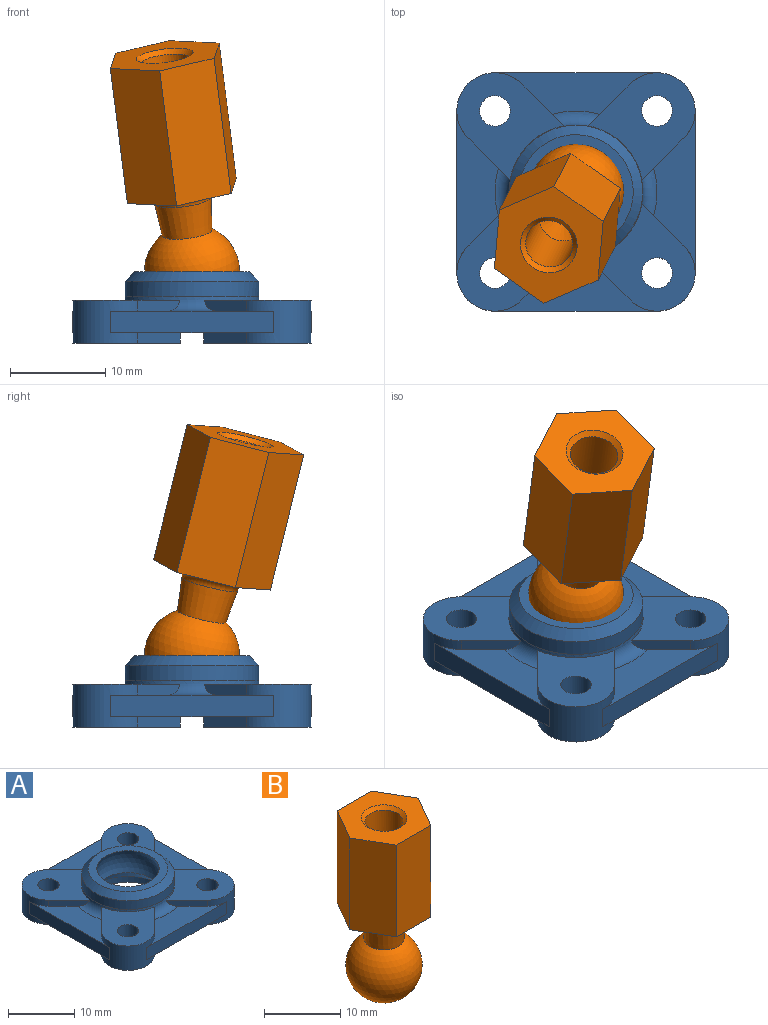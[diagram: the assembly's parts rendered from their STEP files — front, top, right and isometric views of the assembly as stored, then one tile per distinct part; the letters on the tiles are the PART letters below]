
ASSEMBLY  parts=2 mates=1
PART A: 54 faces, bbox 25.1x25.1x7.6 mm
  f0: cylinder r=4mm len=6.83mm, axis (0,0,-1), area 42.4mm2, adj f14,f15,f21,f28,f29,f30,f33,f34
  f1: cylinder r=4mm len=6.83mm, axis (0,0,-1), area 42.4mm2, adj f15,f19,f27,f32,f34,f35,f37,f46
  f2: cylinder r=4mm len=6.83mm, axis (0,0,-1), area 42.4mm2, adj f19,f20,f22,f31,f38,f39,f41,f42
  f3: cylinder r=4mm len=6.83mm, axis (0,0,-1), area 42.4mm2, adj f16,f17,f18,f21,f22,f29,f43,f44
  f4: cone r=5.81mm half-angle=45deg, axis (0,0,-1), area 120.4mm2, adj f12,f21,f22,f23,f24,f25,f26,f34
  f5: cylinder r=7mm len=14mm, axis (0,0,1), area 71.5mm2, adj f6,f7
  f6: cone r=6.5mm half-angle=45deg, axis (0,0,-1), area 57.8mm2, adj f5,f13
  f7: torus R=8.5mm, axis (0,0,-1), area 45.8mm2, adj f5,f14,f15,f16,f17,f18,f19,f20
  f8: cylinder r=1.6mm len=4.5mm, axis (0,0,-1), area 45.2mm2, adj f17,f48
  f9: cylinder r=1.6mm len=4.5mm, axis (0,0,-1), area 45.2mm2, adj f31,f38
  f10: cylinder r=1.6mm len=4.5mm, axis (0,0,-1), area 45.2mm2, adj f32,f37
  f11: cylinder r=1.6mm len=4.5mm, axis (0,0,-1), area 45.2mm2, adj f30,f36
  f12: sphere r=5.11mm, area 130.2mm2, adj f4,f13
  f13: plane 12x12mm, normal (0,0,1), area 43.6mm2, adj f6,f12
  f14: plane 4.54x4.54mm, normal (0.71,-0.71,0), area 6.5mm2, adj f0,f7,f29,f30
  f15: plane 17x4.37mm, normal (0,0,1), area 40.2mm2, adj f0,f1,f7,f27,f28,f52
  f16: plane 4.53x4.53mm, normal (0.71,0.71,0), area 6.5mm2, adj f3,f7,f17,f29
  f17: plane 11.23x11.23mm, normal (0,0,1), area 60.1mm2, adj f3,f7,f8,f16,f18
  f18: plane 4.54x4.54mm, normal (-0.71,-0.71,0), area 6.5mm2, adj f3,f7,f17,f43
  f19: plane 17x4.37mm, normal (0,0,1), area 40.2mm2, adj f1,f2,f7,f41,f47,f51
  f20: plane 4.53x4.53mm, normal (0.71,-0.71,0), area 6.5mm2, adj f2,f7,f31,f43
  f21: plane 17x5.61mm, normal (0,0,-1), area 45.8mm2, adj f0,f3,f4,f33,f45,f53
  f22: plane 17x5.61mm, normal (0,0,-1), area 45.8mm2, adj f2,f3,f4,f42,f44,f50
  f23: cylinder r=7mm len=5.66mm, axis (0,0,-1), area 9.6mm2, adj f4,f35,f37,f46
  f24: cylinder r=7mm len=5.66mm, axis (0,0,-1), area 9.6mm2, adj f4,f38,f39,f42
  f25: cylinder r=7mm len=5.66mm, axis (0,0,-1), area 9.6mm2, adj f4,f44,f45,f48
  f26: cylinder r=7mm len=5.66mm, axis (0,0,-1), area 9.6mm2, adj f4,f33,f36,f40
  f27: plane 4.54x4.54mm, normal (0.71,0.71,0), area 6.5mm2, adj f1,f7,f15,f32
  f28: plane 4.53x4.53mm, normal (-0.71,0.71,0), area 6.5mm2, adj f0,f7,f15,f30
  f29: plane 17x4.37mm, normal (0,0,1), area 40.2mm2, adj f0,f3,f7,f14,f16,f53
  f30: plane 11.23x11.23mm, normal (0,0,1), area 60.1mm2, adj f0,f7,f11,f14,f28
  f31: plane 11.23x11.23mm, normal (0,0,1), area 60.1mm2, adj f2,f7,f9,f20,f41
  f32: plane 11.23x11.23mm, normal (0,0,1), area 60.1mm2, adj f1,f7,f10,f27,f47
  f33: plane 4.44x4.44mm, normal (0.71,-0.71,0), area 7.1mm2, adj f0,f21,f26,f36
  f34: plane 17x5.61mm, normal (0,0,-1), area 45.8mm2, adj f0,f1,f4,f35,f40,f52
  f35: plane 4.44x4.44mm, normal (0.71,0.71,0), area 7.1mm2, adj f1,f23,f34,f37
  f36: plane 11.27x11.27mm, normal (0,0,-1), area 60.5mm2, adj f0,f11,f26,f33,f40
  f37: plane 11.27x11.27mm, normal (0,0,-1), area 60.5mm2, adj f1,f10,f23,f35,f46
  f38: plane 11.27x11.27mm, normal (0,0,-1), area 60.5mm2, adj f2,f9,f24,f39,f42
  f39: plane 4.44x4.44mm, normal (-0.71,0.71,0), area 7.1mm2, adj f2,f24,f38,f49
  f40: plane 4.44x4.44mm, normal (-0.71,0.71,0), area 7.1mm2, adj f0,f26,f34,f36
  f41: plane 4.54x4.54mm, normal (-0.71,0.71,0), area 6.5mm2, adj f2,f7,f19,f31
  f42: plane 4.44x4.44mm, normal (0.71,-0.71,0), area 7.1mm2, adj f2,f22,f24,f38
  f43: plane 17x4.37mm, normal (0,0,1), area 40.2mm2, adj f2,f3,f7,f18,f20,f50
  f44: plane 4.44x4.44mm, normal (-0.71,-0.71,0), area 7.1mm2, adj f3,f22,f25,f48
  f45: plane 4.44x4.44mm, normal (0.71,0.71,0), area 7.1mm2, adj f3,f21,f25,f48
  f46: plane 4.44x4.44mm, normal (-0.71,-0.71,0), area 7.1mm2, adj f1,f23,f37,f49
  f47: plane 4.53x4.53mm, normal (-0.71,-0.71,0), area 6.5mm2, adj f1,f7,f19,f32
  f48: plane 11.27x11.27mm, normal (0,0,-1), area 60.5mm2, adj f3,f8,f25,f44,f45
  f49: plane 17x5.61mm, normal (0,0,-1), area 45.8mm2, adj f1,f2,f4,f39,f46,f51
  f50: plane 17x2.25mm, normal (0,-1,0), area 38.3mm2, adj f2,f3,f22,f43
  f51: plane 17x2.25mm, normal (-1,0,0), area 38.3mm2, adj f1,f2,f19,f49
  f52: plane 17x2.25mm, normal (0,1,0), area 38.3mm2, adj f0,f1,f15,f34
  f53: plane 17x2.25mm, normal (1,0,0), area 38.3mm2, adj f0,f3,f21,f29
PART B: 15 faces, bbox 12.7x11x27.5 mm
  f0: cylinder r=2.5mm len=11.5mm, axis (0,0,-1), area 180.6mm2, adj f1,f2
  f1: cone r=1.25mm half-angle=60deg, axis (0,0,1), area 22.7mm2, adj f0
  f2: cone r=1.5mm half-angle=45deg, axis (0,0,1), area 12.2mm2, adj f0,f13
  f3: cone r=2.54mm half-angle=6deg, axis (0,0,1), area 63mm2, adj f4,f5
  f4: torus R=4.12mm, axis (0,0,-1), area 32.5mm2, adj f3,f14
  f5: sphere r=5mm, area 259.3mm2, adj f3,f6
  f6: plane 6x6mm, normal (0,0,-1), area 28.3mm2, adj f5
  f7: plane 14.7x5.5mm, normal (0.87,-0.5,0), area 93.4mm2, adj f8,f12,f13,f14
  f8: plane 14.7x5.5mm, normal (0.87,0.5,0), area 93.4mm2, adj f7,f9,f13,f14
  f9: plane 14.7x6.35mm, normal (0,1,0), area 93.4mm2, adj f8,f10,f13,f14
  f10: plane 14.7x5.5mm, normal (-0.87,0.5,0), area 93.4mm2, adj f9,f11,f13,f14
  f11: plane 14.7x5.5mm, normal (-0.87,-0.5,0), area 93.4mm2, adj f10,f12,f13,f14
  f12: plane 14.7x6.35mm, normal (0,-1,0), area 93.4mm2, adj f7,f11,f13,f14
  f13: plane 12.7x11mm, normal (0,0,1), area 76.5mm2, adj f2,f7,f8,f9,f10,f11,f12
  f14: plane 12.7x11mm, normal (0,0,-1), area 54.5mm2, adj f4,f7,f8,f9,f10,f11,f12
PLACE A t=(-1.82,-11.01,3.39)mm fixed
PLACE B rot(axis=(0.42,-0.34,0.84),28.8deg) t=(-1.15,-9.7,5.59)mm
MATE ball B.f0 <-> A.f4  axis (-0.12,-0.24,0.96) through (-1.82,-11.01,10.89)mm
